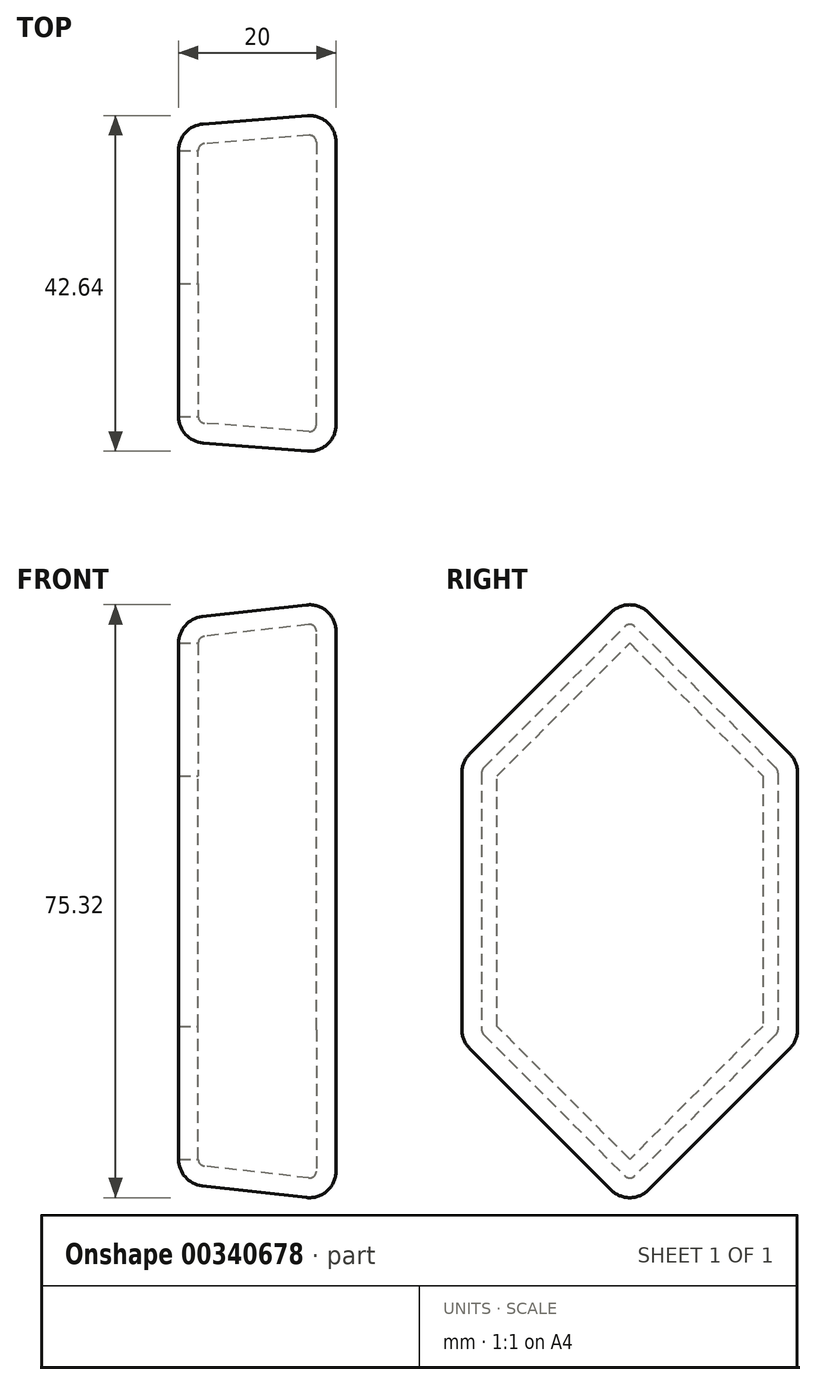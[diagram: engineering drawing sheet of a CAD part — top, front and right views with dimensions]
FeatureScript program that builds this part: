
annotation { "Feature Type Name" : "Feature", "Feature Type Description" : "" }
export const myFeature = defineFeature(function(context is Context, id is Id, definition is map)
    precondition{}
    {
        {
            var Q0;
            Q0=qCreatedBy(makeId("Right.planeOp"),FACE);
            var sketch = newSketch(context, id + "F0", { "sketchPlane" : qUnion([Q0])});
            skLineSegment(sketch, "E0.left", {"start": v(-20, 17.17) * mm, "end": v(-20, -17.17) * mm});
            skLineSegment(sketch, "E0.right", {"start": v(20, 17.17) * mm, "end": v(20, -17.17) * mm});
            skPoint(sketch, "E0.middle", {"position": v(0, 0) * mm});
            skLineSegment(sketch, "E1", {"start": v(0, 37.2) * mm, "end": v(0, -37.2) * mm});
            skLineSegment(sketch, "E2", {"start": v(-20, -17.17) * mm, "end": v(0, -37.2) * mm});
            skLineSegment(sketch, "E3", {"start": v(20, -17.17) * mm, "end": v(0, -37.2) * mm});
            skLineSegment(sketch, "E4", {"start": v(-20, 17.17) * mm, "end": v(0, 37.2) * mm});
            skLineSegment(sketch, "E5", {"start": v(20, 17.17) * mm, "end": v(0, 37.2) * mm});
            skPoint(sketch, "E6.orphan", {"position": v(-20, 37.2) * mm});
            skPoint(sketch, "E7.orphan", {"position": v(-20, -37.2) * mm});
            skPoint(sketch, "E8.orphan", {"position": v(20, -37.2) * mm});
            skPoint(sketch, "E0.bottom.end.orphan", {"position": v(20, 37.2) * mm});
            skSolve(sketch);
        }
        {
            var Q0;
            Q0 = qSketchRegion(id + "F0", true);
            extrude(context, id + "F1", {"entities" : qUnion([Q0]), "depth" : 20 * mm, "hasDraft" : true, "draftAngle" : 0.08 * radian});
        }
        {
            var Q0;
            Q0=makeQuery(id+"F1.opExtrude","CAP_EDGE",EDGE,{"disambiguationData":[OSD([sQuery(id+"F0.wireOp",EDGE,"E2")])],"isStart":false});
            var Q1;
            Q1=makeQuery(id+"F1.opExtrude","SWEPT_FACE",FACE,{"disambiguationData":[OSD([sQuery(id+"F0.wireOp",EDGE,"E0.left")])]});
            var Q2;
            Q2=makeQuery(id+"F1.opExtrude","SWEPT_EDGE",EDGE,{"disambiguationData":[OSD([sQuery(id+"F0.wireOp",EDGE,"E1"),sQuery(id+"F0.wireOp",EDGE,"E2"),sQuery(id+"F0.wireOp",EDGE,"E3")])]});
            var Q3;
            Q3=makeQuery(id+"F1.opExtrude","SWEPT_EDGE",EDGE,{"disambiguationData":[OSD([sQuery(id+"F0.wireOp",EDGE,"E0.left"),sQuery(id+"F0.wireOp",EDGE,"E4")])]});
            var Q4;
            Q4=makeQuery(id+"F1.opExtrude","CAP_EDGE",EDGE,{"disambiguationData":[OSD([sQuery(id+"F0.wireOp",EDGE,"E4")])],"isStart":true});
            var Q5;
            Q5=makeQuery(id+"F1.opExtrude","CAP_FACE",FACE,{"disambiguationData":[OSD([sQuery(id+"F0.wireOp",EDGE,"E0.left"),sQuery(id+"F0.wireOp",EDGE,"E0.right"),sQuery(id+"F0.wireOp",EDGE,"E2"),sQuery(id+"F0.wireOp",EDGE,"E3"),sQuery(id+"F0.wireOp",EDGE,"E4"),sQuery(id+"F0.wireOp",EDGE,"E5")])],"isStart":false});
            var Q6;
            Q6=makeQuery(id+"F1.opExtrude","SWEPT_FACE",FACE,{"disambiguationData":[OSD([sQuery(id+"F0.wireOp",EDGE,"E2")])]});
            var Q7;
            Q7=makeQuery(id+"F1.opExtrude","SWEPT_EDGE",EDGE,{"disambiguationData":[OSD([sQuery(id+"F0.wireOp",EDGE,"E1"),sQuery(id+"F0.wireOp",EDGE,"E4"),sQuery(id+"F0.wireOp",EDGE,"E5")])]});
            var Q8;
            Q8=makeQuery(id+"F1.opExtrude","SWEPT_FACE",FACE,{"disambiguationData":[OSD([sQuery(id+"F0.wireOp",EDGE,"E4")])]});
            var Q9;
            Q9=makeQuery(id+"F1.opExtrude","SWEPT_EDGE",EDGE,{"disambiguationData":[OSD([sQuery(id+"F0.wireOp",EDGE,"E0.left"),sQuery(id+"F0.wireOp",EDGE,"E2")])]});
            var Q10;
            Q10=makeQuery(id+"F1.opExtrude","SWEPT_FACE",FACE,{"disambiguationData":[OSD([sQuery(id+"F0.wireOp",EDGE,"E3")])]});
            var Q11;
            Q11=makeQuery(id+"F1.opExtrude","CAP_FACE",FACE,{"disambiguationData":[OSD([sQuery(id+"F0.wireOp",EDGE,"E0.left"),sQuery(id+"F0.wireOp",EDGE,"E0.right"),sQuery(id+"F0.wireOp",EDGE,"E2"),sQuery(id+"F0.wireOp",EDGE,"E3"),sQuery(id+"F0.wireOp",EDGE,"E4"),sQuery(id+"F0.wireOp",EDGE,"E5")])],"isStart":true});
            var Q12;
            Q12=makeQuery(id+"F1.opExtrude","CAP_EDGE",EDGE,{"disambiguationData":[OSD([sQuery(id+"F0.wireOp",EDGE,"E4")])],"isStart":false});
            var Q13;
            Q13=makeQuery(id+"F1.opExtrude","CAP_EDGE",EDGE,{"disambiguationData":[OSD([sQuery(id+"F0.wireOp",EDGE,"E2")])],"isStart":true});
            var Q14;
            Q14=makeQuery(id+"F1.opExtrude","SWEPT_EDGE",EDGE,{"disambiguationData":[OSD([sQuery(id+"F0.wireOp",EDGE,"E0.right"),sQuery(id+"F0.wireOp",EDGE,"E3")])]});
            var Q15;
            Q15=makeQuery(id+"F1.opExtrude","SWEPT_FACE",FACE,{"disambiguationData":[OSD([sQuery(id+"F0.wireOp",EDGE,"E5")])]});
            var Q16;
            Q16=makeQuery(id+"F1.opExtrude","CAP_EDGE",EDGE,{"disambiguationData":[OSD([sQuery(id+"F0.wireOp",EDGE,"E0.left")])],"isStart":true});
            var Q17;
            Q17=makeQuery(id+"F1.opExtrude","CAP_EDGE",EDGE,{"disambiguationData":[OSD([sQuery(id+"F0.wireOp",EDGE,"E0.left")])],"isStart":false});
            var Q18;
            Q18=makeQuery(id+"F1.opExtrude","CAP_EDGE",EDGE,{"disambiguationData":[OSD([sQuery(id+"F0.wireOp",EDGE,"E3")])],"isStart":false});
            var Q19;
            Q19=makeQuery(id+"F1.opExtrude","SWEPT_EDGE",EDGE,{"disambiguationData":[OSD([sQuery(id+"F0.wireOp",EDGE,"E0.right"),sQuery(id+"F0.wireOp",EDGE,"E5")])]});
            var Q20;
            Q20=makeQuery(id+"F1.opExtrude","SWEPT_FACE",FACE,{"disambiguationData":[OSD([sQuery(id+"F0.wireOp",EDGE,"E0.right")])]});
            var Q21;
            Q21=makeQuery(id+"F1.opExtrude","CAP_EDGE",EDGE,{"disambiguationData":[OSD([sQuery(id+"F0.wireOp",EDGE,"E5")])],"isStart":true});
            var Q22;
            Q22=makeQuery(id+"F1.opExtrude","CAP_EDGE",EDGE,{"disambiguationData":[OSD([sQuery(id+"F0.wireOp",EDGE,"E5")])],"isStart":false});
            var Q23;
            Q23=makeQuery(id+"F1.opExtrude","CAP_EDGE",EDGE,{"disambiguationData":[OSD([sQuery(id+"F0.wireOp",EDGE,"E3")])],"isStart":true});
            var Q24;
            Q24=makeQuery(id+"F1.opExtrude","CAP_EDGE",EDGE,{"disambiguationData":[OSD([sQuery(id+"F0.wireOp",EDGE,"E0.right")])],"isStart":true});
            var Q25;
            Q25=makeQuery(id+"F1.opExtrude","CAP_EDGE",EDGE,{"disambiguationData":[OSD([sQuery(id+"F0.wireOp",EDGE,"E0.right")])],"isStart":false});
            fillet(context, id + "F2", {"entities" : qUnion([Q0, Q1, Q2, Q3, Q4, Q5, Q6, Q7, Q8, Q9, Q10, Q11, Q12, Q13, Q14, Q15, Q16, Q17, Q18, Q19, Q20, Q21, Q22, Q23, Q24, Q25]), "radius" : 3.37 * mm, "tangentPropagation" : true, "allowEdgeOverflow" : false});
        }
        {
            var Q0;
            Q0=makeQuery(id+"F1.opExtrude","CAP_FACE",FACE,{"disambiguationData":[OSD([sQuery(id+"F0.wireOp",EDGE,"E0.left"),sQuery(id+"F0.wireOp",EDGE,"E0.right"),sQuery(id+"F0.wireOp",EDGE,"E2"),sQuery(id+"F0.wireOp",EDGE,"E3"),sQuery(id+"F0.wireOp",EDGE,"E4"),sQuery(id+"F0.wireOp",EDGE,"E5")])],"isStart":true});
            shell(context, id + "F3", {"entities" : qUnion([Q0]), "thickness" : 2.5 * mm});
        }
    });
